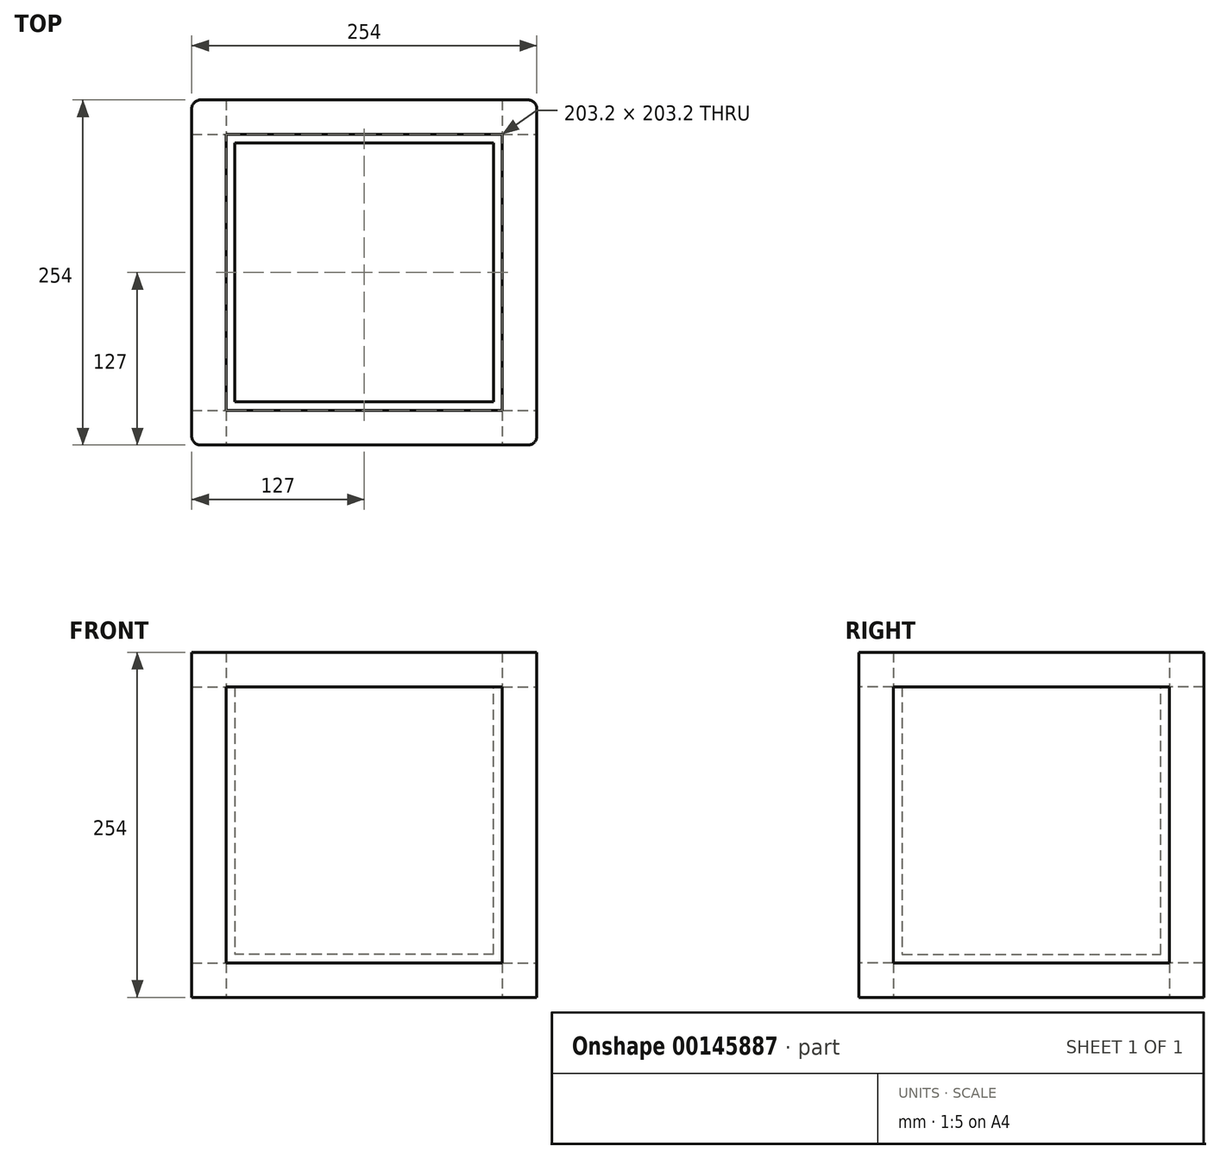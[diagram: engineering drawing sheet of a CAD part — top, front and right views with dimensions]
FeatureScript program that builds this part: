
annotation { "Feature Type Name" : "Feature", "Feature Type Description" : "" }
export const myFeature = defineFeature(function(context is Context, id is Id, definition is map)
    precondition{}
    {
        {
            var Q0;
            Q0=qCreatedBy(makeId("Top.planeOp"),FACE);
            var sketch = newSketch(context, id + "F0", { "sketchPlane" : qUnion([Q0])});
            skLineSegment(sketch, "E0.bottom", {"start": v(120.65, 127) * mm, "end": v(-120.65, 127) * mm});
            skLineSegment(sketch, "E0.top", {"start": v(120.65, -127) * mm, "end": v(-120.65, -127) * mm});
            skLineSegment(sketch, "E0.left", {"start": v(127, 120.65) * mm, "end": v(127, -120.65) * mm});
            skLineSegment(sketch, "E0.right", {"start": v(-127, 120.65) * mm, "end": v(-127, -120.65) * mm});
            skPoint(sketch, "E0.middle", {"position": v(0, 0) * mm});
            skPoint(sketch, "E1.visualSharp", {"position": v(-127, 127) * mm});
            skArc(sketch, "E1.filletArc", {"start": v(-120.65, 127) * mm, "mid": v(-125.14, 125.14) * mm, "end": v(-127, 120.65) * mm});
            skPoint(sketch, "E2.visualSharp", {"position": v(-127, -127) * mm});
            skArc(sketch, "E2.filletArc", {"start": v(-127, -120.65) * mm, "mid": v(-125.14, -125.14) * mm, "end": v(-120.65, -127) * mm});
            skPoint(sketch, "E3.visualSharp", {"position": v(127, -127) * mm});
            skArc(sketch, "E3.filletArc", {"start": v(120.65, -127) * mm, "mid": v(125.14, -125.14) * mm, "end": v(127, -120.65) * mm});
            skPoint(sketch, "E4.visualSharp", {"position": v(127, 127) * mm});
            skArc(sketch, "E4.filletArc", {"start": v(127, 120.65) * mm, "mid": v(125.14, 125.14) * mm, "end": v(120.65, 127) * mm});
            skLineSegment(sketch, "E5.bottom", {"start": v(101.6, 101.6) * mm, "end": v(-101.6, 101.6) * mm});
            skLineSegment(sketch, "E5.top", {"start": v(101.6, -101.6) * mm, "end": v(-101.6, -101.6) * mm});
            skLineSegment(sketch, "E5.left", {"start": v(101.6, 101.6) * mm, "end": v(101.6, -101.6) * mm});
            skLineSegment(sketch, "E5.right", {"start": v(-101.6, 101.6) * mm, "end": v(-101.6, -101.6) * mm});
            skSolve(sketch);
        }
        {
            var Q0;
            Q0 = qSketchRegion(id + "F0", true);
            extrude(context, id + "F1", {"entities" : qUnion([Q0]), "endBound" : BoundingType.SYMMETRIC, "depth" : 254 * mm});
        }
        {
            var Q0;
            Q0=makeQuery(id+"F1.opExtrude","SWEPT_FACE",FACE,{"disambiguationData":[OSD([sQuery(id+"F0.wireOp",EDGE,"E0.top")])]});
            var sketch = newSketch(context, id + "F2", { "sketchPlane" : qUnion([Q0])});
            skLineSegment(sketch, "E6.bottom", {"start": v(101.6, 101.6) * mm, "end": v(-101.6, 101.6) * mm});
            skLineSegment(sketch, "E6.top", {"start": v(101.6, -101.6) * mm, "end": v(-101.6, -101.6) * mm});
            skLineSegment(sketch, "E6.left", {"start": v(101.6, 101.6) * mm, "end": v(101.6, -101.6) * mm});
            skLineSegment(sketch, "E6.right", {"start": v(-101.6, 101.6) * mm, "end": v(-101.6, -101.6) * mm});
            skPoint(sketch, "E6.middle", {"position": v(0, 0) * mm});
            skSolve(sketch);
        }
        {
            var Q0;
            Q0 = qSketchRegion(id + "F2", true);
            extrude(context, id + "F3", {"entities" : qUnion([Q0]), "operationType" : NewBodyOperationType.REMOVE, "endBound" : BoundingType.THROUGH_ALL, "oppositeDirection" : true, "depth" : 25.4 * mm});
        }
        {
            var Q0;
            Q0=makeQuery(id+"F1.opExtrude","SWEPT_FACE",FACE,{"disambiguationData":[OSD([sQuery(id+"F0.wireOp",EDGE,"E0.left")])]});
            var sketch = newSketch(context, id + "F4", { "sketchPlane" : qUnion([Q0])});
            skLineSegment(sketch, "E7.bottom", {"start": v(101.6, 101.6) * mm, "end": v(-101.6, 101.6) * mm});
            skLineSegment(sketch, "E7.top", {"start": v(101.6, -101.6) * mm, "end": v(-101.6, -101.6) * mm});
            skLineSegment(sketch, "E7.left", {"start": v(101.6, 101.6) * mm, "end": v(101.6, -101.6) * mm});
            skLineSegment(sketch, "E7.right", {"start": v(-101.6, 101.6) * mm, "end": v(-101.6, -101.6) * mm});
            skPoint(sketch, "E7.middle", {"position": v(0, 0) * mm});
            skSolve(sketch);
        }
        {
            var Q0;
            Q0 = qSketchRegion(id + "F4", true);
            extrude(context, id + "F5", {"entities" : qUnion([Q0]), "operationType" : NewBodyOperationType.REMOVE, "endBound" : BoundingType.THROUGH_ALL, "oppositeDirection" : true, "depth" : 254 * mm});
        }
        {
            var Q0;
            Q0=makeQuery(id+"F3.boolean.opBoolean","COPY",FACE,{"disambiguationData":[TD([makeQuery(id+"F1.opExtrude","SWEPT_FACE",FACE,{"disambiguationData":[OSD([sQuery(id+"F0.wireOp",EDGE,"E0.top")])]})])],"derivedFrom":makeQuery(id+"F3.opExtrude","SWEPT_FACE",FACE,{"disambiguationData":[OSD([sQuery(id+"F2.wireOp",EDGE,"E6.top")])]})});
            var sketch = newSketch(context, id + "F6", { "sketchPlane" : qUnion([Q0])});
            skLineSegment(sketch, "E8.bottom", {"start": v(101.6, -101.6) * mm, "end": v(-101.6, -101.6) * mm});
            skLineSegment(sketch, "E8.top", {"start": v(101.6, 101.6) * mm, "end": v(-101.6, 101.6) * mm});
            skLineSegment(sketch, "E8.left", {"start": v(101.6, -101.6) * mm, "end": v(101.6, 101.6) * mm});
            skLineSegment(sketch, "E8.right", {"start": v(-101.6, -101.6) * mm, "end": v(-101.6, 101.6) * mm});
            skSolve(sketch);
        }
        {
            var Q0;
            Q0 = qSketchRegion(id + "F6", true);
            extrude(context, id + "F7", {"entities" : qUnion([Q0]), "depth" : 6.35 * mm});
        }
        {
            var Q0;
            Q0=makeQuery(id+"F5.boolean.opBoolean","COPY",FACE,{"disambiguationData":[TD([makeQuery(id+"F1.opExtrude","SWEPT_FACE",FACE,{"disambiguationData":[OSD([sQuery(id+"F0.wireOp",EDGE,"E0.left")])]})])],"derivedFrom":makeQuery(id+"F5.opExtrude","SWEPT_FACE",FACE,{"disambiguationData":[OSD([sQuery(id+"F4.wireOp",EDGE,"E7.right")])]})});
            var sketch = newSketch(context, id + "F8", { "sketchPlane" : qUnion([Q0])});
            skLineSegment(sketch, "E9.bottom", {"start": v(101.6, 101.6) * mm, "end": v(-101.6, 101.6) * mm});
            skLineSegment(sketch, "E9.top", {"start": v(101.6, -101.6) * mm, "end": v(-101.6, -101.6) * mm});
            skLineSegment(sketch, "E9.left", {"start": v(101.6, 101.6) * mm, "end": v(101.6, -101.6) * mm});
            skLineSegment(sketch, "E9.right", {"start": v(-101.6, 101.6) * mm, "end": v(-101.6, -101.6) * mm});
            skPoint(sketch, "E9.middle", {"position": v(0, 0) * mm});
            skSolve(sketch);
        }
        {
            var Q0;
            Q0 = qSketchRegion(id + "F8", true);
            extrude(context, id + "F9", {"entities" : qUnion([Q0]), "operationType" : NewBodyOperationType.ADD, "depth" : 6.35 * mm});
        }
        {
            var Q0;
            {var subQ0=makeQuery(id+"F3.opExtrude","SWEPT_FACE",FACE,{"disambiguationData":[OSD([sQuery(id+"F2.wireOp",EDGE,"E6.left")])]});var subQ1=makeQuery(id+"F1.opExtrude","SWEPT_FACE",FACE,{"disambiguationData":[OSD([sQuery(id+"F0.wireOp",EDGE,"E5.left")])]});var subQ4=makeQuery(id+"F1.opExtrude","SWEPT_FACE",FACE,{"disambiguationData":[OSD([sQuery(id+"F0.wireOp",EDGE,"E0.bottom")])]});Q0=makeQuery(id+"F5.boolean.opBoolean","SPLIT",FACE,{"disambiguationData":[TD([subQ4])],"derivedFrom":makeQuery(id+"F3.boolean.opBoolean","MERGE",FACE,{"derivedFrom":[subQ1,subQ0]})});}
            var sketch = newSketch(context, id + "F10", { "sketchPlane" : qUnion([Q0])});
            skLineSegment(sketch, "E10.bottom", {"start": v(-101.6, -101.6) * mm, "end": v(101.6, -101.6) * mm});
            skLineSegment(sketch, "E10.top", {"start": v(-101.6, 101.6) * mm, "end": v(101.6, 101.6) * mm});
            skLineSegment(sketch, "E10.left", {"start": v(-101.6, -101.6) * mm, "end": v(-101.6, 101.6) * mm});
            skLineSegment(sketch, "E10.right", {"start": v(101.6, -101.6) * mm, "end": v(101.6, 101.6) * mm});
            skPoint(sketch, "E10.middle", {"position": v(0, 0) * mm});
            skSolve(sketch);
        }
        {
            var Q0;
            Q0 = qSketchRegion(id + "F10", true);
            extrude(context, id + "F11", {"entities" : qUnion([Q0]), "operationType" : NewBodyOperationType.ADD, "depth" : 6.35 * mm});
        }
        {
            var Q0;
            Q0=makeQuery(id+"F5.boolean.opBoolean","COPY",FACE,{"disambiguationData":[TD([makeQuery(id+"F1.opExtrude","SWEPT_FACE",FACE,{"disambiguationData":[OSD([sQuery(id+"F0.wireOp",EDGE,"E0.right")])]})])],"derivedFrom":makeQuery(id+"F5.opExtrude","SWEPT_FACE",FACE,{"disambiguationData":[OSD([sQuery(id+"F4.wireOp",EDGE,"E7.left")])]})});
            var sketch = newSketch(context, id + "F12", { "sketchPlane" : qUnion([Q0])});
            skLineSegment(sketch, "E11.bottom", {"start": v(101.6, 101.6) * mm, "end": v(-101.6, 101.6) * mm});
            skLineSegment(sketch, "E11.top", {"start": v(101.6, -101.6) * mm, "end": v(-101.6, -101.6) * mm});
            skLineSegment(sketch, "E11.left", {"start": v(101.6, 101.6) * mm, "end": v(101.6, -101.6) * mm});
            skLineSegment(sketch, "E11.right", {"start": v(-101.6, 101.6) * mm, "end": v(-101.6, -101.6) * mm});
            skPoint(sketch, "E11.middle", {"position": v(0, 0) * mm});
            skSolve(sketch);
        }
        {
            var Q0;
            Q0 = qSketchRegion(id + "F12", true);
            extrude(context, id + "F13", {"entities" : qUnion([Q0]), "operationType" : NewBodyOperationType.ADD, "depth" : 6.35 * mm});
        }
        {
            var Q0;
            {var subQ0=makeQuery(id+"F3.opExtrude","SWEPT_FACE",FACE,{"disambiguationData":[OSD([sQuery(id+"F2.wireOp",EDGE,"E6.right")])]});var subQ1=makeQuery(id+"F1.opExtrude","SWEPT_FACE",FACE,{"disambiguationData":[OSD([sQuery(id+"F0.wireOp",EDGE,"E5.right")])]});var subQ4=makeQuery(id+"F1.opExtrude","SWEPT_FACE",FACE,{"disambiguationData":[OSD([sQuery(id+"F0.wireOp",EDGE,"E0.top")])]});Q0=makeQuery(id+"F5.boolean.opBoolean","SPLIT",FACE,{"disambiguationData":[TD([subQ4])],"derivedFrom":makeQuery(id+"F3.boolean.opBoolean","MERGE",FACE,{"derivedFrom":[subQ1,subQ0]})});}
            var sketch = newSketch(context, id + "F14", { "sketchPlane" : qUnion([Q0])});
            skLineSegment(sketch, "E12.bottom", {"start": v(101.6, -101.6) * mm, "end": v(-101.6, -101.6) * mm});
            skLineSegment(sketch, "E12.top", {"start": v(101.6, 101.6) * mm, "end": v(-101.6, 101.6) * mm});
            skLineSegment(sketch, "E12.left", {"start": v(101.6, -101.6) * mm, "end": v(101.6, 101.6) * mm});
            skLineSegment(sketch, "E12.right", {"start": v(-101.6, -101.6) * mm, "end": v(-101.6, 101.6) * mm});
            skPoint(sketch, "E12.middle", {"position": v(0, 0) * mm});
            skSolve(sketch);
        }
        {
            var Q0;
            Q0 = qSketchRegion(id + "F14", true);
            extrude(context, id + "F15", {"entities" : qUnion([Q0]), "operationType" : NewBodyOperationType.ADD, "depth" : 6.35 * mm});
        }
    });
